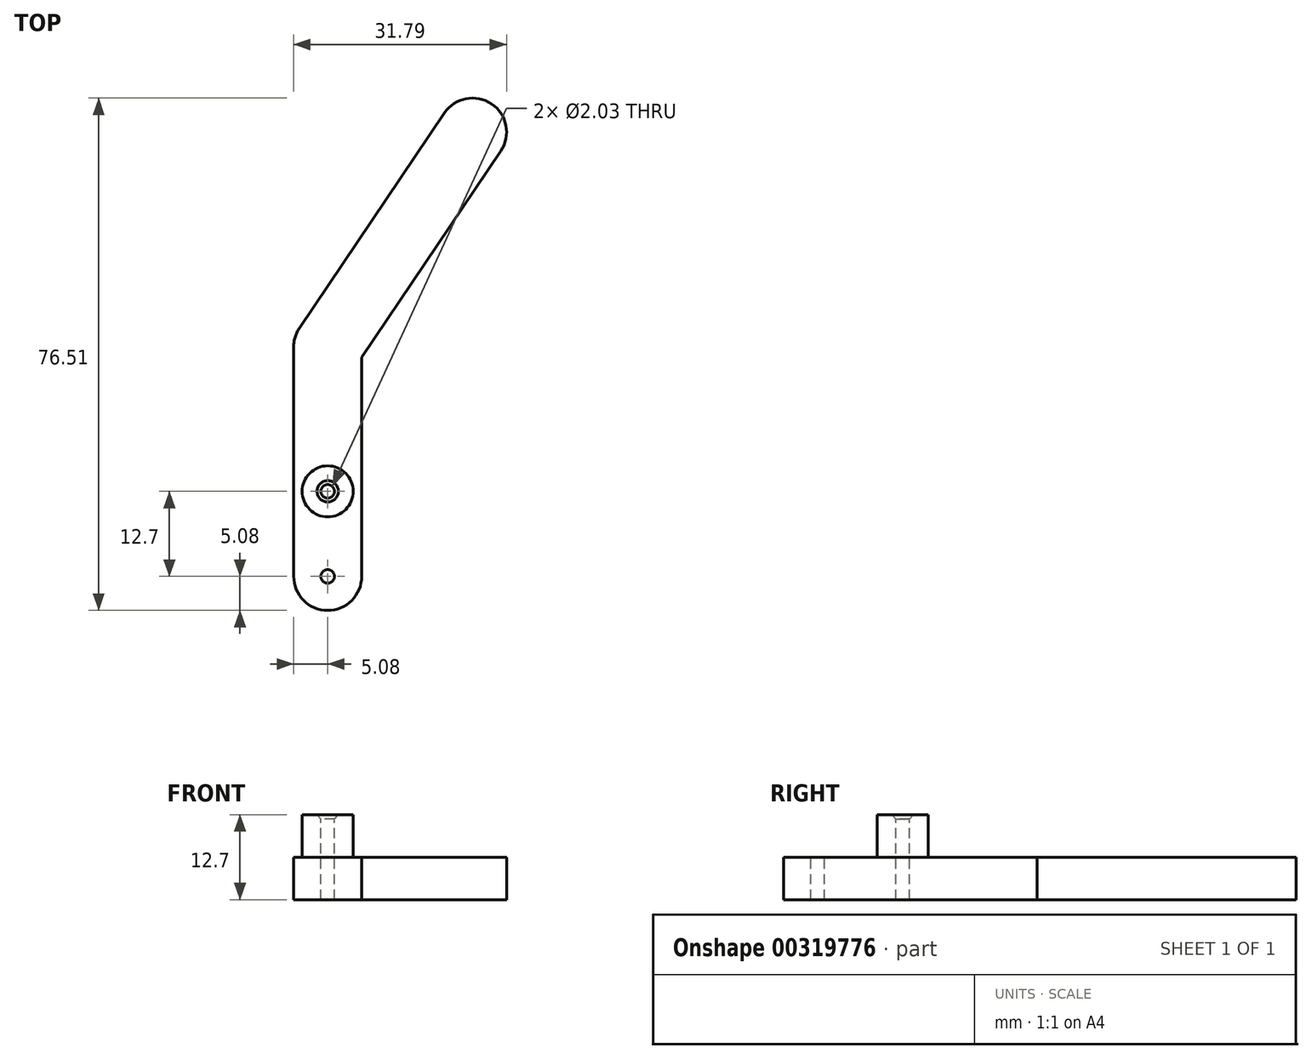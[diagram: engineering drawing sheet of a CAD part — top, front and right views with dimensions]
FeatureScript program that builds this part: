
annotation { "Feature Type Name" : "Feature", "Feature Type Description" : "" }
export const myFeature = defineFeature(function(context is Context, id is Id, definition is map)
    precondition{}
    {
        {
            var Q0;
            Q0=qCreatedBy(makeId("Top.planeOp"),FACE);
            var sketch = newSketch(context, id + "F0", { "sketchPlane" : qUnion([Q0])});
            skLineSegment(sketch, "E0", {"start": v(0, 0) * mm, "end": v(0, 12.7) * mm});
            skLineSegment(sketch, "E1", {"start": v(0, 12.7) * mm, "end": v(0, 34.3) * mm});
            skLineSegment(sketch, "E2", {"start": v(0, 34.3) * mm, "end": v(21.63, 66.35) * mm});
            skArc(sketch, "E3.0.startCap", {"start": v(5.08, 0) * mm, "mid": v(0, -5.08) * mm, "end": v(-5.08, 0) * mm});
            skArc(sketch, "E3.0.endCap", {"start": v(-5.08, 12.7) * mm, "mid": v(0, 17.78) * mm, "end": v(5.08, 12.7) * mm});
            skLineSegment(sketch, "E3.0.left", {"start": v(-5.08, 0) * mm, "end": v(-5.08, 12.7) * mm});
            skLineSegment(sketch, "E3.0.right", {"start": v(5.08, 0) * mm, "end": v(5.08, 12.7) * mm});
            skArc(sketch, "E3.1.startCap", {"start": v(5.08, 12.7) * mm, "mid": v(0, 7.62) * mm, "end": v(-5.08, 12.7) * mm});
            skArc(sketch, "E3.1.endCap", {"start": v(-5.08, 34.3) * mm, "mid": v(0, 39.37) * mm, "end": v(5.08, 34.3) * mm});
            skLineSegment(sketch, "E3.1.left", {"start": v(-5.08, 12.7) * mm, "end": v(-5.08, 34.3) * mm});
            skLineSegment(sketch, "E3.1.right", {"start": v(5.08, 12.7) * mm, "end": v(5.08, 34.3) * mm});
            skArc(sketch, "E3.2.startCap", {"start": v(4.21, 31.45) * mm, "mid": v(-2.84, 30.08) * mm, "end": v(-4.21, 37.13) * mm});
            skArc(sketch, "E3.2.endCap", {"start": v(17.41, 69.2) * mm, "mid": v(24.47, 70.56) * mm, "end": v(25.84, 63.51) * mm});
            skLineSegment(sketch, "E3.2.left", {"start": v(-4.21, 37.13) * mm, "end": v(17.41, 69.2) * mm});
            skLineSegment(sketch, "E3.2.right", {"start": v(4.21, 31.45) * mm, "end": v(25.84, 63.51) * mm});
            skSolve(sketch);
        }
        {
            var Q0;
            Q0 = qSketchRegion(id + "F0", true);
            extrude(context, id + "F1", {"entities" : qUnion([Q0]), "depth" : 6.35 * mm});
        }
        {
            var Q0;
            Q0=makeQuery(id+"F1.opExtrude","CAP_FACE",FACE,{"disambiguationData":[OSD([sQuery(id+"F0.wireOp",EDGE,"E3.0.startCap"),sQuery(id+"F0.wireOp",EDGE,"E3.0.left"),sQuery(id+"F0.wireOp",EDGE,"E3.0.right"),sQuery(id+"F0.wireOp",EDGE,"E3.1.left"),sQuery(id+"F0.wireOp",EDGE,"E3.1.right"),sQuery(id+"F0.wireOp",EDGE,"E3.2.startCap"),sQuery(id+"F0.wireOp",EDGE,"E3.2.endCap"),sQuery(id+"F0.wireOp",EDGE,"E3.2.left"),sQuery(id+"F0.wireOp",EDGE,"E3.2.right")])],"isStart":false});
            var sketch = newSketch(context, id + "F2", { "sketchPlane" : qUnion([Q0])});
            skCircle(sketch, "E4", {"center": v(0, 12.7) * mm, "radius": 3.81 * mm});
            skSolve(sketch);
        }
        {
            var Q0;
            Q0 = qSketchRegion(id + "F2", true);
            extrude(context, id + "F3", {"entities" : qUnion([Q0]), "operationType" : NewBodyOperationType.ADD, "depth" : 6.35 * mm});
        }
        {
            var Q0;
            Q0=makeQuery(id+"F3.opExtrude","CAP_FACE",FACE,{"disambiguationData":[OSD([sQuery(id+"F2.wireOp",EDGE,"E4")])],"isStart":false});
            var sketch = newSketch(context, id + "F4", { "sketchPlane" : qUnion([Q0])});
            skPoint(sketch, "E5", {"position": v(0, 12.7) * mm});
            skSolve(sketch);
        }
        {
            var Q0;
            Q0=sQuery(id+"F4.wireOp",VERTEX,"E5");
            var Q1;
            Q1=makeQuery(id+"F1.opExtrude","SWEPT_BODY",BODY,{"disambiguationData":[OSD([sQuery(id+"F0.wireOp",EDGE,"E3.0.startCap"),sQuery(id+"F0.wireOp",EDGE,"E3.0.left"),sQuery(id+"F0.wireOp",EDGE,"E3.0.right"),sQuery(id+"F0.wireOp",EDGE,"E3.1.left"),sQuery(id+"F0.wireOp",EDGE,"E3.1.right"),sQuery(id+"F0.wireOp",EDGE,"E3.2.startCap"),sQuery(id+"F0.wireOp",EDGE,"E3.2.endCap"),sQuery(id+"F0.wireOp",EDGE,"E3.2.left"),sQuery(id+"F0.wireOp",EDGE,"E3.2.right")])]});
            hole(context, id + "F5", {"style" : HoleStyle.C_SINK, "endStyle" : HoleEndStyle.THROUGH, "holeDiameter" : 2.03 * mm, "cSinkDiameter" : 3.17 * mm, "cSinkAngle" : 82 * degree, "tappedDepth" : 12.7 * mm, "tapClearance" : 3, "locations" : qUnion([Q0]), "scope" : qUnion([Q1])});
        }
        {
            var Q0;
            Q0=makeQuery(id+"F1.opExtrude","CAP_FACE",FACE,{"disambiguationData":[OSD([sQuery(id+"F0.wireOp",EDGE,"E3.0.startCap"),sQuery(id+"F0.wireOp",EDGE,"E3.0.left"),sQuery(id+"F0.wireOp",EDGE,"E3.0.right"),sQuery(id+"F0.wireOp",EDGE,"E3.1.left"),sQuery(id+"F0.wireOp",EDGE,"E3.1.right"),sQuery(id+"F0.wireOp",EDGE,"E3.2.startCap"),sQuery(id+"F0.wireOp",EDGE,"E3.2.endCap"),sQuery(id+"F0.wireOp",EDGE,"E3.2.left"),sQuery(id+"F0.wireOp",EDGE,"E3.2.right")])],"isStart":false});
            var sketch = newSketch(context, id + "F6", { "sketchPlane" : qUnion([Q0])});
            skPoint(sketch, "E6", {"position": v(0, 0) * mm});
            skSolve(sketch);
        }
        {
            var Q0;
            Q0=sQuery(id+"F6.wireOp",VERTEX,"E6");
            var Q1;
            Q1=makeQuery(id+"F1.opExtrude","SWEPT_BODY",BODY,{"disambiguationData":[OSD([sQuery(id+"F0.wireOp",EDGE,"E3.0.startCap"),sQuery(id+"F0.wireOp",EDGE,"E3.0.left"),sQuery(id+"F0.wireOp",EDGE,"E3.0.right"),sQuery(id+"F0.wireOp",EDGE,"E3.1.left"),sQuery(id+"F0.wireOp",EDGE,"E3.1.right"),sQuery(id+"F0.wireOp",EDGE,"E3.2.startCap"),sQuery(id+"F0.wireOp",EDGE,"E3.2.endCap"),sQuery(id+"F0.wireOp",EDGE,"E3.2.left"),sQuery(id+"F0.wireOp",EDGE,"E3.2.right")])]});
            hole(context, id + "F7", {"style" : HoleStyle.SIMPLE, "endStyle" : HoleEndStyle.THROUGH, "holeDiameter" : 2.03 * mm, "tappedDepth" : 12.7 * mm, "tapClearance" : 3, "locations" : qUnion([Q0]), "scope" : qUnion([Q1])});
        }
    });
